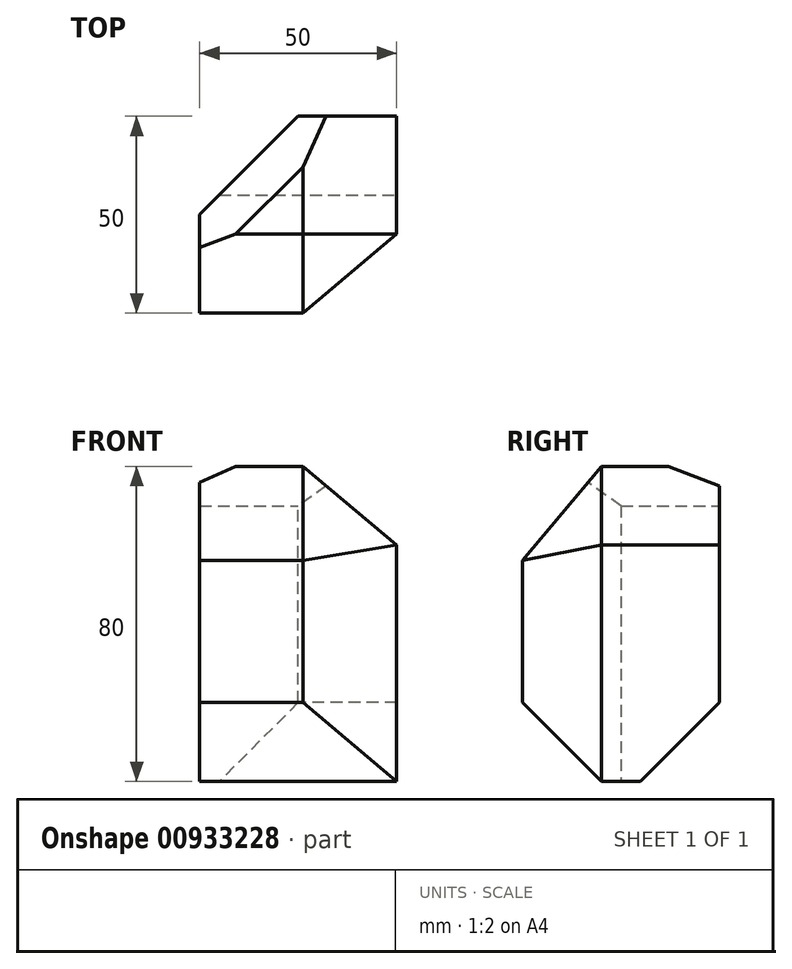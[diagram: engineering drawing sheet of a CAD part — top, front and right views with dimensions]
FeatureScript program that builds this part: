
annotation { "Feature Type Name" : "Feature", "Feature Type Description" : "" }
export const myFeature = defineFeature(function(context is Context, id is Id, definition is map)
    precondition{}
    {
        {
            var Q0;
            Q0=qCreatedBy(makeId("Top.planeOp"),FACE);
            var sketch = newSketch(context, id + "F0", { "sketchPlane" : qUnion([Q0])});
            skLineSegment(sketch, "E0.bottom", {"start": v(-25, 25) * mm, "end": v(25, 25) * mm});
            skLineSegment(sketch, "E0.top", {"start": v(-25, -25) * mm, "end": v(25, -25) * mm});
            skLineSegment(sketch, "E0.left", {"start": v(-25, 25) * mm, "end": v(-25, -25) * mm});
            skLineSegment(sketch, "E0.right", {"start": v(25, 25) * mm, "end": v(25, -25) * mm});
            skPoint(sketch, "E1", {"position": v(0, 25) * mm});
            skPoint(sketch, "E2", {"position": v(25, 0) * mm});
            skSolve(sketch);
        }
        {
            var Q0;
            Q0 = qSketchRegion(id + "F0", true);
            extrude(context, id + "F1", {"entities" : qUnion([Q0]), "depth" : 80 * mm, "offsetDistance" : 25 * mm});
        }
        {
            var Q0;
            Q0=makeQuery(id+"F1.opExtrude","SWEPT_EDGE",EDGE,{"disambiguationData":[OSD([sQuery(id+"F0.wireOp",EDGE,"E0.top"),sQuery(id+"F0.wireOp",EDGE,"E0.right")])]});
            var Q1;
            Q1=makeQuery(id+"F1.opExtrude","CAP_EDGE",EDGE,{"disambiguationData":[OSD([sQuery(id+"F0.wireOp",EDGE,"E0.right")])],"isStart":false});
            var Q2;
            Q2=makeQuery(id+"F1.opExtrude","CAP_EDGE",EDGE,{"disambiguationData":[OSD([sQuery(id+"F0.wireOp",EDGE,"E0.top")])],"isStart":false});
            chamfer(context, id + "F2", {"entities" : qUnion([Q0, Q1, Q2]), "chamferType" : ChamferType.OFFSET_ANGLE, "width" : 20 * mm, "oppositeDirection" : false, "angle" : 50 * degree, "tangentPropagation" : true});
        }
        {
            var Q0;
            Q0=makeQuery(id+"F1.opExtrude","SWEPT_EDGE",EDGE,{"disambiguationData":[OSD([sQuery(id+"F0.wireOp",EDGE,"E0.bottom"),sQuery(id+"F0.wireOp",EDGE,"E0.left")])]});
            chamfer(context, id + "F3", {"entities" : qUnion([Q0]), "width" : 25 * mm, "tangentPropagation" : true});
        }
        {
            var Q0;
            {var subQ0=sQuery(id+"F0.wireOp",EDGE,"E0.left");var subQ1=sQuery(id+"F0.wireOp",EDGE,"E0.bottom");Q0=makeQuery(id+"F3.opChamfer","BLEND_EDGE",EDGE,{"blendedFrom":[makeQuery(id+"F1.opExtrude","SWEPT_EDGE",EDGE,{"disambiguationData":[OSD([subQ1,subQ0])]}),makeQuery(id+"F1.opExtrude","CAP_FACE",FACE,{"disambiguationData":[OSD([subQ1,sQuery(id+"F0.wireOp",EDGE,"E0.top"),subQ0,sQuery(id+"F0.wireOp",EDGE,"E0.right")])],"isStart":false})],"blendedInto":[makeQuery(id+"F1.opExtrude","CAP_FACE",FACE,{"disambiguationData":[OSD([subQ1,sQuery(id+"F0.wireOp",EDGE,"E0.top"),subQ0,sQuery(id+"F0.wireOp",EDGE,"E0.right")])],"isStart":false})]});}
            chamfer(context, id + "F4", {"entities" : qUnion([Q0]), "width" : 10 * mm, "tangentPropagation" : true});
        }
        {
            var Q0;
            Q0=makeQuery(id+"F1.opExtrude","CAP_EDGE",EDGE,{"disambiguationData":[OSD([sQuery(id+"F0.wireOp",EDGE,"E0.bottom")])],"isStart":true});
            var Q1;
            Q1=makeQuery(id+"F1.opExtrude","CAP_EDGE",EDGE,{"disambiguationData":[OSD([sQuery(id+"F0.wireOp",EDGE,"E0.top")])],"isStart":true});
            chamfer(context, id + "F5", {"entities" : qUnion([Q0, Q1]), "width" : 20 * mm, "tangentPropagation" : true});
        }
    });
